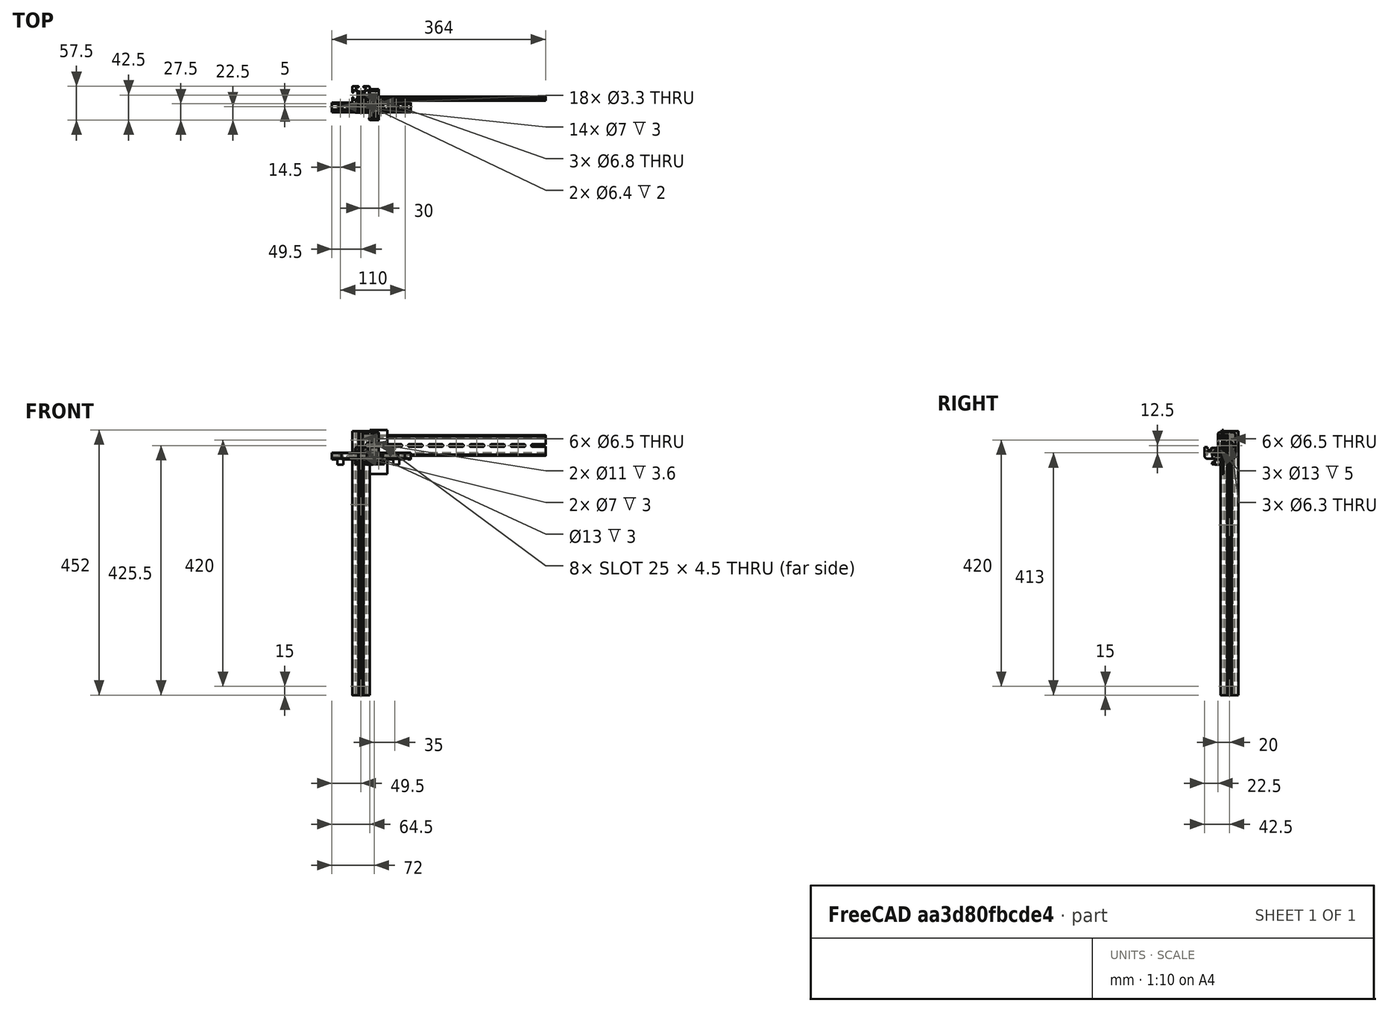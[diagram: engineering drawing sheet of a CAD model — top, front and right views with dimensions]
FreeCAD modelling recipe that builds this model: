
FCSTD DOCUMENT  (FreeCAD 0.19R24291 (Git))
Label: back-bottom-pannel
License: Other
LicenseURL: GPL3
objects: Part::Box×38, Part::Feature×36, Part::Cut×25, Part::MultiFuse×25, Part::Chamfer×19, Part::Cylinder×13, Part::Extrusion×7, Part::Refine×4
note: 167 computed .brp shape members not serialized (recipe doc carries the construction recipe); baked Part::Feature solids carry a one-line shape summary decoded from their .brp

FEATURE [Part::Box] Box  label="Cube"
  AttacherType = Attacher::AttachEngine3D
  Height = 45
  Length = 29
  Placement = pos=(-14,0,0) rot=(0,0,1;0rad)
  Width = 10
FEATURE [Part::Box] Box001  label="Cube001"
  AttacherType = Attacher::AttachEngine3D
  Height = 35.5
  Length = 29
  Placement = pos=(-11,2.5,4.75) rot=(0,0,1;0rad)
  Width = 7.5
FEATURE [Part::Cut] Cut
  Base = -> Box
  Tool = -> Box001
FEATURE [Part::Chamfer] Chamfer
  Base = -> Cut
  Edges = 5 edges r=2: [Edge1,Edge2,Edge4,Edge5,Edge7]
FEATURE [Part::Box] Box002  label="Cube002"
  AttacherType = Attacher::AttachEngine3D
  Height = 23
  Length = 27
  Placement = pos=(-12,2.5,11) rot=(0,0,1;0rad)
  Width = 6
FEATURE [Part::Chamfer] Chamfer001
  Base = -> Box002
  Edges = 2 edges r=1: [Edge11,Edge12]
FEATURE [Part::Box] Box003  label="Cube003"
  AttacherType = Attacher::AttachEngine3D
  Height = 4.75
  Length = 7.8
  Placement = pos=(-3.9,9,0) rot=(0,0,1;0rad)
  Width = 3
FEATURE [Part::Box] Box004  label="Cube004"
  AttacherType = Attacher::AttachEngine3D
  Height = 4.75
  Length = 7.8
  Placement = pos=(-3.9,9,40.25) rot=(0,0,1;0rad)
  Width = 3
FEATURE [Part::MultiFuse] Fusion
  Shapes = -> [Box004,Box003,Chamfer001]
FEATURE [Part::Chamfer] Chamfer002
  Base = -> Fusion
  Edges = 4 edges r=0.4: [Edge3,Edge7,Edge15,Edge19]
FEATURE [Part::MultiFuse] Fusion001
  Shapes = -> [Chamfer002,Chamfer]
FEATURE [Part::Cylinder] Cylinder
  Angle = 360
  AttacherType = Attacher::AttachEngine3D
  Height = 10
  Placement = pos=(0,5e-15,22.5) rot=(-1,0,0;1.5708rad)
  Radius = 2.15
FEATURE [Part::Cylinder] Cylinder001
  Angle = 360
  AttacherType = Attacher::AttachEngine3D
  Height = 10
  Placement = pos=(0,-6,22.5) rot=(-1,0,0;1.5708rad)
  Radius = 5.5
FEATURE [Part::Cut] Cut001
  Base = -> Fusion001
  Tool = -> Cylinder
FEATURE [Part::Cut] Cut002
  Base = -> Cut001
  Tool = -> Cylinder001
FEATURE [Part::Chamfer] Chamfer003
  Base = -> Cut002
  Edges = 1 edges r=0.4: [Edge82]
FEATURE [Part::Feature] Chamfer003001  label="Chamfer004"
  shape: bbox 29 x 12 x 45 mm, 39 faces (baked)
FEATURE [Part::Box] Box005  label="Cube005"
  AttacherType = Attacher::AttachEngine3D
  Height = 20
  Length = 35
  Placement = pos=(-25,0,0) rot=(0,0,1;0rad)
  Width = 5
FEATURE [Part::Cylinder] Cylinder002
  Angle = 360
  AttacherType = Attacher::AttachEngine3D
  Height = 10
  Placement = pos=(-15,-7,10) rot=(-1,0,0;1.5708rad)
  Radius = 6.5
FEATURE [Part::Box] Box006  label="Cube006"
  AttacherType = Attacher::AttachEngine3D
  Height = 20
  Length = 7.8
  Placement = pos=(-18.9,4,0) rot=(0,0,1;0rad)
  Width = 2
FEATURE [Part::Cylinder] Cylinder003
  Angle = 360
  AttacherType = Attacher::AttachEngine3D
  Height = 10
  Placement = pos=(-15,2e-15,10) rot=(-1,0,0;1.5708rad)
  Radius = 3.15
FEATURE [Part::Box] Box007  label="Cube007"
  AttacherType = Attacher::AttachEngine3D
  Height = 20
  Length = 9.5
  Placement = pos=(0.5,5,0) rot=(0,0,1;0rad)
  Width = 2
FEATURE [Part::Feature] Common001003002002001  label="din-309mm"
  Placement = pos=(147,-10,60.5) rot=(-1,0,0;1.5708rad)
  shape: bbox 305 x 7.5 x 35 mm, 68 faces (baked)
FEATURE [Part::Feature] Cut008004003004014002002002  label="3030-450mm-back002-drill"
  Placement = pos=(-15,20,-403) rot=(0,0,1;0rad)
  shape: bbox 30 x 30 x 450 mm, 181 faces (baked)
FEATURE [Part::Box] Box008  label="Cube008"
  AttacherType = Attacher::AttachEngine3D
  Height = 75
  Length = 30
  Placement = pos=(0,7,-26) rot=(0,0,1;0rad)
  Width = 3
FEATURE [Part::Box] Box009  label="Cube009"
  AttacherType = Attacher::AttachEngine3D
  Height = 45
  Length = 15
  Placement = pos=(0,10,0) rot=(0,0,1;0rad)
  Width = 20
FEATURE [Part::Box] Box010  label="Cube010"
  AttacherType = Attacher::AttachEngine3D
  Height = 23.5
  Length = 15
  Placement = pos=(0,11.75,10.75) rot=(0,0,1;0rad)
  Width = 7.75
FEATURE [Part::Box] Box011  label="Cube011"
  AttacherType = Attacher::AttachEngine3D
  Height = 35.5
  Length = 15
  Placement = pos=(0,10,4.75) rot=(0,0,1;0rad)
  Width = 7.75
FEATURE [Part::Box] Box012  label="Cube012"
  AttacherType = Attacher::AttachEngine3D
  Height = 4.75
  Length = 10
  Placement = pos=(-1,16.1,0) rot=(0,0,1;0rad)
  Width = 7.8
FEATURE [Part::Box] Box013  label="Cube013"
  AttacherType = Attacher::AttachEngine3D
  Height = 4.75
  Length = 10
  Placement = pos=(-1,16.1,40.25) rot=(0,0,1;0rad)
  Width = 7.8
FEATURE [Part::Box] Box014  label="Cube014"
  AttacherType = Attacher::AttachEngine3D
  Height = 23.5
  Length = 10
  Placement = pos=(-1,16.1,10.75) rot=(0,0,1;0rad)
  Width = 7.8
FEATURE [Part::MultiFuse] Fusion005
  Shapes = -> [Box014,Box012,Box013]
FEATURE [Part::Chamfer] Chamfer003008
  Base = -> Fusion005
  Edges = 6 edges r=1: [Edge2,Edge4,Edge14,Edge16,Edge26,Edge28]
FEATURE [Part::Cylinder] Cylinder004
  Angle = 360
  AttacherType = Attacher::AttachEngine3D
  Height = 18
  Placement = pos=(10,20,22.5) rot=(0,1,0;1.5708rad)
  Radius = 6.5
FEATURE [Part::Cylinder] Cylinder005
  Angle = 360
  AttacherType = Attacher::AttachEngine3D
  Height = 18
  Placement = pos=(-3.5,20,22.5) rot=(0,1,0;1.5708rad)
  Radius = 3.15
FEATURE [Part::Chamfer] Chamfer003009
  Base = -> Box005
  Edges = 4 edges r=2: [Edge2,Edge4,Edge6,Edge8]
FEATURE [Part::Chamfer] Chamfer003010
  Base = -> Box007
  Edges = 2 edges r=2: [Edge6,Edge8]
FEATURE [Part::Chamfer] Chamfer003011
  Base = -> Chamfer003009
  Edges = 8 edges r=1: [Edge1,Edge5,Edge6,Edge7,Edge8,Edge9,Edge10,Edge11]
FEATURE [Part::MultiFuse] Fusion007
  Shapes = -> [Chamfer003010,Chamfer003011,Box006]
FEATURE [Part::Feature] Cut008004003004014002002005003001  label="panel-inner-clip001"
  shape: bbox 35 x 7 x 20 mm, 27 faces (baked)
FEATURE [Part::Cut] Cut008004003004014002002005003002
  Base = -> Box009
  Tool = -> Box011
FEATURE [Part::MultiFuse] Fusion008
  Shapes = -> [Box010,Cut008004003004014002002005003002]
FEATURE [Part::Chamfer] Chamfer003012
  Base = -> Fusion008
  Edges = 4 edges r=0.4: [Edge39,Edge40,Edge41,Edge42]
FEATURE [Part::Chamfer] Chamfer003013
  Base = -> Chamfer003012
  Edges = 2 edges r=1: [Edge50,Edge54]
FEATURE [Part::Chamfer] Chamfer003014
  Base = -> Chamfer003013
  Edges = 2 edges r=3: [Edge57,Edge58]
FEATURE [Part::MultiFuse] Fusion009
  Shapes = -> [Chamfer003008,Chamfer003014]
FEATURE [Part::Cut] Cut008004003004014002002005003003
  Base = -> Fusion009
  Tool = -> Cylinder004
FEATURE [Part::Cut] Cut008004003004014002002005003004  label="din-stopper"
  Base = -> Cut008004003004014002002005003003
  Tool = -> Cylinder005
FEATURE [Part::Feature] Cut008004003004014002002005003004001  label="din-stopper001"
  shape: bbox 16 x 20 x 45 mm, 43 faces (baked)
FEATURE [Part::Box] Box015  label="Cube015"
  AttacherType = Attacher::AttachEngine3D
  Height = 15
  Length = 10
  Placement = pos=(-5,-10,0) rot=(0,0,1;0rad)
  Width = 4.5
FEATURE [Part::Box] Box016  label="Cube016"
  AttacherType = Attacher::AttachEngine3D
  Height = 5
  Length = 10
  Placement = pos=(-5,-9.5,0) rot=(0,0,1;0rad)
  Width = 16.5
FEATURE [Part::Box] Box017  label="Cube017"
  AttacherType = Attacher::AttachEngine3D
  Height = 2
  Length = 10
  Placement = pos=(-5,-3.9,-1) rot=(0,0,1;0rad)
  Width = 7.8
FEATURE [Part::Chamfer] Chamfer003015
  Base = -> Box017
  Edges = 1 edges r=1: [Edge9]
FEATURE [Part::Cylinder] Cylinder006
  Angle = 360
  AttacherType = Attacher::AttachEngine3D
  Height = 10
  Placement = pos=(0,0,-4) rot=(0,0,1;0rad)
  Radius = 1.65
FEATURE [Part::Cylinder] Cylinder007
  Angle = 360
  AttacherType = Attacher::AttachEngine3D
  Height = 10
  Placement = pos=(0,0,2) rot=(0,0,1;0rad)
  Radius = 3.5
FEATURE [Part::MultiFuse] Fusion011
  Shapes = -> [Cylinder007,Cylinder006]
FEATURE [Part::Cylinder] Cylinder008
  Angle = 360
  AttacherType = Attacher::AttachEngine3D
  Height = 10
  Placement = pos=(0,-12,10) rot=(-1,0,0;1.5708rad)
  Radius = 1.9
FEATURE [Part::Feature] Chamfer003017001_cs  label="gasket-support-profile"
  shape: bbox 3e-07 x 16.5 x 11 mm, 0 faces, 0 solids (baked)
FEATURE [Part::MultiFuse] Fusion012
  Shapes = -> [Box015,Box016,Chamfer003015]
FEATURE [Part::Chamfer] Chamfer003016
  Base = -> Fusion012
  Edges = 3 edges r=0.4: [Edge9,Edge16,Edge32]
FEATURE [Part::Chamfer] Chamfer003017
  Base = -> Chamfer003016
  Edges = 2 edges r=2: [Edge10,Edge27]
FEATURE [Part::Cut] Cut008004003004014002002005003004002
  Base = -> Chamfer003017
  Tool = -> Cylinder008
FEATURE [Part::Cut] Cut008004003004014002002005003004003  label="back-panel-support"
  Base = -> Cut008004003004014002002005003004002
  Tool = -> Fusion011
FEATURE [Part::Feature] Cut008004003004014002002005003004003001  label="back-panel-support001"
  shape: bbox 10 x 17 x 16 mm, 21 faces (baked)
FEATURE [Part::Feature] Chamfer003017001_cs001  label="gasket-support-profile001"
  shape: bbox 3e-07 x 16.5 x 11 mm, 0 faces, 0 solids (baked)
FEATURE [Part::Feature] Fusion011001  label="m3-slot"
  shape: bbox 7 x 7 x 16 mm, 5 faces (baked)
FEATURE [Part::Feature] Fusion011002  label="m3-slot001"
  shape: bbox 7 x 7 x 16 mm, 5 faces (baked)
FEATURE [Part::Feature] Fusion011003  label="m3-slot002"
  Placement = pos=(-50,0,0) rot=(0,0,1;0rad)
  shape: bbox 7 x 7 x 16 mm, 5 faces (baked)
FEATURE [Part::Feature] Fusion011004  label="m3-slot003"
  Placement = pos=(45,0,0) rot=(0,0,1;0rad)
  shape: bbox 7 x 7 x 16 mm, 5 faces (baked)
FEATURE [Part::Extrusion] Extrude
  Base = -> Chamfer003017001_cs001
  Dir = (1,0,0)
  DirMode = 2
  FaceMakerClass = Part::FaceMakerBullseye
  LengthFwd = 119
  LengthRev = 0
  Placement = pos=(-59.5,0,0) rot=(0,0,1;0rad)
  Solid = true
  Symmetric = false
FEATURE [Part::Feature] Chamfer003017001_cs002  label="gasket-support-profile002"
  shape: bbox 3e-07 x 16.5 x 11 mm, 0 faces, 0 solids (baked)
FEATURE [Part::Extrusion] Extrude001
  Base = -> Chamfer003017001_cs002
  Dir = (1,0,0)
  DirMode = 2
  FaceMakerClass = Part::FaceMakerBullseye
  LengthFwd = 39
  LengthRev = 0
  Placement = pos=(-19.5,0,0) rot=(0,0,1;0rad)
  Solid = true
  Symmetric = false
FEATURE [Part::Feature] Fusion011006  label="m3-slot004"
  Placement = pos=(-10,0,0) rot=(0,0,1;0rad)
  shape: bbox 7 x 7 x 16 mm, 5 faces (baked)
FEATURE [Part::Feature] Fusion011007  label="m3-slot005"
  Placement = pos=(10,0,0) rot=(0,0,1;0rad)
  shape: bbox 7 x 7 x 16 mm, 5 faces (baked)
FEATURE [Part::MultiFuse] Fusion011008
  Shapes = -> [Fusion011007,Fusion011006]
FEATURE [Part::Cut] Cut008004003004014002002005003004003002002  label="gasket-support-40mm"
  Base = -> Extrude001
  Tool = -> Fusion011008
FEATURE [Part::Feature] Chamfer003017001_cs003  label="gasket-support-profile003"
  shape: bbox 3e-07 x 16.5 x 11 mm, 0 faces, 0 solids (baked)
FEATURE [Part::Extrusion] Extrude002
  Base = -> Chamfer003017001_cs003
  Dir = (1,0,0)
  DirMode = 2
  FaceMakerClass = Part::FaceMakerBullseye
  LengthFwd = 44
  LengthRev = 0
  Placement = pos=(-17,0,0) rot=(0,0,1;0rad)
  Solid = true
  Symmetric = false
FEATURE [Part::Feature] Fusion011009  label="m3-slot006"
  Placement = pos=(15,0,0) rot=(0,0,1;0rad)
  shape: bbox 7 x 7 x 16 mm, 5 faces (baked)
FEATURE [Part::Feature] Fusion011010  label="m3-slot007"
  Placement = pos=(-15,0,0) rot=(0,0,1;0rad)
  shape: bbox 7 x 7 x 16 mm, 5 faces (baked)
FEATURE [Part::Cut] Cut008004003004014002002005003004003002003001002
  Base = -> Fusion007
  Tool = -> Cylinder003
FEATURE [Part::Cut] Cut008004003004014002002005003004003002003001003  label="back-btm-pannel-inner-clip"
  Base = -> Cut008004003004014002002005003004003002003001002
  Tool = -> Cylinder002
FEATURE [Part::Refine] Cut008004003004014002002005003004003002003001003001  label="back-btm-pannel-inner-clip001"
  Source = -> Cut008004003004014002002005003004003002003001003
FEATURE [Part::Feature] Cut008004003004014002002005003004003002003001003001001  label="back-btm-pannel-inner-clip002"
  shape: bbox 35 x 7 x 20 mm, 27 faces (baked)
FEATURE [Part::Box] Box018  label="Cube018"
  AttacherType = Attacher::AttachEngine3D
  Height = 5
  Length = 40
  Placement = pos=(-20,0,0) rot=(0,0,1;0rad)
  Width = 15
FEATURE [Part::Box] Box019  label="Cube019"
  AttacherType = Attacher::AttachEngine3D
  Height = 9
  Length = 40
  Placement = pos=(-20,12,1) rot=(0,0,1;0rad)
  Width = 4.5
FEATURE [Part::Chamfer] Chamfer003018
  Base = -> Box019
  Edges = 1 edges r=1.5: [Edge11]
FEATURE [Part::Chamfer] Chamfer003019
  Base = -> Chamfer003018
  Edges = 2 edges r=3: [Edge2,Edge11]
FEATURE [Part::Chamfer] Chamfer003020
  Base = -> Chamfer003019
  Edges = 5 edges r=1: [Edge3,Edge11,Edge15,Edge17,Edge18]
FEATURE [Part::Chamfer] Chamfer003021
  Base = -> Box018
  Edges = 2 edges r=2: [Edge1,Edge5]
FEATURE [Part::Chamfer] Chamfer003022
  Base = -> Chamfer003021
  Edges = 5 edges r=1: [Edge1,Edge5,Edge6,Edge7,Edge8]
FEATURE [Part::Cylinder] Cylinder009
  Angle = 360
  AttacherType = Attacher::AttachEngine3D
  Height = 10
  Placement = pos=(15,5,0) rot=(0,0,1;0rad)
  Radius = 1.65
FEATURE [Part::Cylinder] Cylinder010
  Angle = 360
  AttacherType = Attacher::AttachEngine3D
  Height = 10
  Placement = pos=(-15,5,0) rot=(0,0,1;0rad)
  Radius = 1.65
FEATURE [Part::MultiFuse] Fusion011012
  Shapes = -> [Chamfer003022,Chamfer003020]
FEATURE [Part::Cylinder] Cylinder011
  Angle = 360
  AttacherType = Attacher::AttachEngine3D
  Height = 10
  Placement = pos=(15,5,3) rot=(0,0,1;0rad)
  Radius = 3.2
FEATURE [Part::Cylinder] Cylinder012
  Angle = 360
  AttacherType = Attacher::AttachEngine3D
  Height = 10
  Placement = pos=(-15,5,3) rot=(0,0,1;0rad)
  Radius = 3.2
FEATURE [Part::MultiFuse] Fusion011013
  Shapes = -> [Cylinder012,Cylinder011,Cylinder010,Cylinder009]
FEATURE [Part::Cut] Cut008004003004014002002005003004003002003001003001002
  Base = -> Fusion011012
  Tool = -> Fusion011013
FEATURE [Part::Refine] Cut008004003004014002002005003004003002003001003001002001
  Source = -> Cut008004003004014002002005003004003002003001003001002
FEATURE [Part::Feature] Cut008004003004014002002005003004003002003001003001002001001
  shape: bbox 40 x 16.5 x 10 mm, 30 faces (baked)
FEATURE [Part::Feature] Extrude002001
  Placement = pos=(-27,0,0) rot=(0,0,1;0rad)
  shape: bbox 44 x 16.5 x 11 mm, 17 faces (baked)
FEATURE [Part::MultiFuse] Fusion011014
  Shapes = -> [Extrude002001,Extrude002]
FEATURE [Part::MultiFuse] Fusion011015
  Shapes = -> [Fusion011010,Fusion011009]
FEATURE [Part::Cut] Cut008004003004014002002005003004003002003001003001002001002  label="gasket-54mm"
  Base = -> Fusion011014
  Tool = -> Fusion011015
FEATURE [Part::Feature] Extrude002002
  Placement = pos=(-64.5,0,0) rot=(0,0,1;0rad)
  shape: bbox 119 x 16.5 x 11 mm, 17 faces (baked)
FEATURE [Part::MultiFuse] Fusion011016
  Shapes = -> [Extrude002002,Extrude]
FEATURE [Part::MultiFuse] Fusion011017
  Shapes = -> [Fusion011004,Fusion011002,Fusion011003]
FEATURE [Part::Cut] Cut008004003004014002002005003004003002003001003001002001002002  label="gasket-124mm"
  Base = -> Fusion011016
  Tool = -> Fusion011017
FEATURE [Part::Feature] Chamfer003017001_cs004  label="gasket-support-profile004"
  shape: bbox 3e-07 x 16.5 x 11 mm, 0 faces, 0 solids (baked)
FEATURE [Part::Extrusion] Extrude002003
  Base = -> Chamfer003017001_cs004
  Dir = (1,0,0)
  DirMode = 2
  FaceMakerClass = Part::FaceMakerBullseye
  LengthFwd = 38
  LengthRev = 0
  Placement = pos=(-19,0,0) rot=(0,0,1;0rad)
  Solid = true
  Symmetric = false
FEATURE [Part::Feature] Fusion011019  label="m3-slot009"
  Placement = pos=(10,0,0) rot=(0,0,1;0rad)
  shape: bbox 7 x 7 x 16 mm, 5 faces (baked)
FEATURE [Part::Feature] Fusion011020  label="m3-slot010"
  Placement = pos=(-10,0,0) rot=(0,0,1;0rad)
  shape: bbox 7 x 7 x 16 mm, 5 faces (baked)
FEATURE [Part::MultiFuse] Fusion011021
  Shapes = -> [Fusion011020,Fusion011019]
FEATURE [Part::Cut] Cut008004003004014002002005003004003002003001003001002001002002002  label="gasket-38mm"
  Base = -> Extrude002003
  Tool = -> Fusion011021
FEATURE [Part::Feature] Fusion011022  label="m3-slot011"
  shape: bbox 7 x 7 x 16 mm, 5 faces (baked)
FEATURE [Part::Feature] Chamfer003017001_cs005  label="gasket-support-profile005"
  shape: bbox 3e-07 x 16.5 x 11 mm, 0 faces, 0 solids (baked)
FEATURE [Part::Extrusion] Extrude002004
  Base = -> Chamfer003017001_cs005
  Dir = (1,0,0)
  DirMode = 2
  FaceMakerClass = Part::FaceMakerBullseye
  LengthFwd = 97
  LengthRev = 0
  Placement = pos=(-48.5,0,0) rot=(0,0,1;0rad)
  Solid = true
  Symmetric = false
FEATURE [Part::Feature] Fusion011023  label="m3-slot012"
  Placement = pos=(35,0,0) rot=(0,0,1;0rad)
  shape: bbox 7 x 7 x 16 mm, 5 faces (baked)
FEATURE [Part::Feature] Fusion011024  label="m3-slot013"
  Placement = pos=(-35,0,0) rot=(0,0,1;0rad)
  shape: bbox 7 x 7 x 16 mm, 5 faces (baked)
FEATURE [Part::MultiFuse] Fusion011025
  Shapes = -> [Fusion011023,Fusion011024,Fusion011022]
FEATURE [Part::Cut] Cut008004003004014002002005003004003002003001003001002001002002003  label="gasket-97mm"
  Base = -> Extrude002004
  Tool = -> Fusion011025
FEATURE [Part::Feature] Fusion011026  label="m3-slot014"
  Placement = pos=(3,0,0) rot=(0,0,1;0rad)
  shape: bbox 7 x 7 x 16 mm, 5 faces (baked)
FEATURE [Part::Feature] Chamfer003017001_cs006  label="gasket-support-profile006"
  shape: bbox 3e-07 x 16.5 x 11 mm, 0 faces, 0 solids (baked)
FEATURE [Part::Feature] Fusion011027  label="m3-slot015"
  Placement = pos=(19,0,0) rot=(0,0,1;0rad)
  shape: bbox 7 x 7 x 16 mm, 5 faces (baked)
FEATURE [Part::Extrusion] Extrude002005
  Base = -> Chamfer003017001_cs006
  Dir = (1,0,0)
  DirMode = 2
  FaceMakerClass = Part::FaceMakerBullseye
  LengthFwd = 22
  LengthRev = 0
  Solid = true
  Symmetric = false
FEATURE [Part::MultiFuse] Fusion011028
  Shapes = -> [Fusion011026,Fusion011027]
FEATURE [Part::Cut] Cut008004003004014002002005003004003002003001003001002001002002004  label="gasket-22mm"
  Base = -> Extrude002005
  Tool = -> Fusion011028
FEATURE [Part::Feature] Chamfer003017001_cs007  label="gasket-support-profile007"
  shape: bbox 3e-07 x 16.5 x 11 mm, 0 faces, 0 solids (baked)
FEATURE [Part::Extrusion] Extrude002006
  Base = -> Chamfer003017001_cs007
  Dir = (1,0,0)
  DirMode = 2
  FaceMakerClass = Part::FaceMakerBullseye
  LengthFwd = 70
  LengthRev = 0
  Solid = true
  Symmetric = false
FEATURE [Part::Feature] Fusion011029  label="m3-slot016"
  Placement = pos=(10,0,0) rot=(0,0,1;0rad)
  shape: bbox 7 x 7 x 16 mm, 5 faces (baked)
FEATURE [Part::Feature] Fusion011030  label="m3-slot017"
  Placement = pos=(60,0,0) rot=(0,0,1;0rad)
  shape: bbox 7 x 7 x 16 mm, 5 faces (baked)
FEATURE [Part::MultiFuse] Fusion011031
  Shapes = -> [Fusion011029,Fusion011030]
FEATURE [Part::Cut] Cut008004003004014002002005003004003002003001003001002001002002005  label="gasket-70mm"
  Base = -> Extrude002006
  Tool = -> Fusion011031
FEATURE [Part::Box] Box020  label="Cube020"
  AttacherType = Attacher::AttachEngine3D
  Height = 10
  Length = 10
  Placement = pos=(-5,-5,-10) rot=(0,0,1;0rad)
  Width = 10
FEATURE [Part::Box] Box021  label="Cube021"
  AttacherType = Attacher::AttachEngine3D
  Height = 10
  Length = 10
  Placement = pos=(30,-5,-10) rot=(0,0,1;0rad)
  Width = 10
FEATURE [Part::Box] Box022  label="Cube022"
  AttacherType = Attacher::AttachEngine3D
  Height = 10
  Length = 10
  Placement = pos=(55,-5,-10) rot=(0,0,1;0rad)
  Width = 10
FEATURE [Part::Box] Box023  label="Cube023"
  AttacherType = Attacher::AttachEngine3D
  Height = 10
  Length = 10
  Placement = pos=(5,-5,-10) rot=(0,0,1;0rad)
  Width = 10
FEATURE [Part::MultiFuse] Fusion011032
  Shapes = -> [Box023,Box022]
FEATURE [Part::Cut] Cut008004003004014002002005003004003002003001003001002001002002006  label="gasket-70mm-cut"
  Base = -> Cut008004003004014002002005003004003002003001003001002001002002005
  Tool = -> Fusion011032
FEATURE [Part::Box] Box024  label="Cube024"
  AttacherType = Attacher::AttachEngine3D
  Height = 10
  Length = 10
  Placement = pos=(-40,-5,-10) rot=(0,0,1;0rad)
  Width = 10
FEATURE [Part::MultiFuse] Fusion011033
  Shapes = -> [Box024,Box021,Box020]
FEATURE [Part::Cut] Cut008004003004014002002005003004003002003001003001002001002002007  label="gasket-97mm-cut"
  Base = -> Cut008004003004014002002005003004003002003001003001002001002002003
  Tool = -> Fusion011033
FEATURE [Part::Box] Box025  label="Cube025"
  AttacherType = Attacher::AttachEngine3D
  Height = 10
  Length = 10
  Placement = pos=(-55,-5,-10) rot=(0,0,1;0rad)
  Width = 10
FEATURE [Part::Box] Box026  label="Cube026"
  AttacherType = Attacher::AttachEngine3D
  Height = 10
  Length = 10
  Placement = pos=(40,-5,-10) rot=(0,0,1;0rad)
  Width = 10
FEATURE [Part::Box] Box027  label="Cube027"
  AttacherType = Attacher::AttachEngine3D
  Height = 10
  Length = 10
  Placement = pos=(-5,-5,-10) rot=(0,0,1;0rad)
  Width = 10
FEATURE [Part::Box] Box028  label="Cube028"
  AttacherType = Attacher::AttachEngine3D
  Height = 10
  Length = 10
  Placement = pos=(-55,-5,-10) rot=(0,0,1;0rad)
  Width = 10
FEATURE [Part::Box] Box029  label="Cube029"
  AttacherType = Attacher::AttachEngine3D
  Height = 10
  Length = 10
  Placement = pos=(40,-5,-10) rot=(0,0,1;0rad)
  Width = 10
FEATURE [Part::Box] Box030  label="Cube030"
  AttacherType = Attacher::AttachEngine3D
  Height = 10
  Length = 10
  Placement = pos=(-5,-5,-10) rot=(0,0,1;0rad)
  Width = 10
FEATURE [Part::MultiFuse] Fusion011034
  Shapes = -> [Box028,Box029,Box030]
FEATURE [Part::Cut] Cut008004003004014002002005003004003002003001003001002001002002008  label="gasket-124mm-cut"
  Base = -> Cut008004003004014002002005003004003002003001003001002001002002
  Tool = -> Fusion011034
FEATURE [Part::Box] Box031  label="Cube031"
  AttacherType = Attacher::AttachEngine3D
  Height = 10
  Length = 10
  Placement = pos=(10,-5,-10) rot=(0,0,1;0rad)
  Width = 10
FEATURE [Part::Box] Box032  label="Cube032"
  AttacherType = Attacher::AttachEngine3D
  Height = 10
  Length = 10
  Placement = pos=(-20,-5,-10) rot=(0,0,1;0rad)
  Width = 10
FEATURE [Part::MultiFuse] Fusion011035
  Shapes = -> [Box031,Box032]
FEATURE [Part::Cut] Cut008004003004014002002005003004003002003001003001002001002002009  label="gasket-54mm-cut"
  Base = -> Cut008004003004014002002005003004003002003001003001002001002
  Tool = -> Fusion011035
FEATURE [Part::Box] Box033  label="Cube033"
  AttacherType = Attacher::AttachEngine3D
  Height = 10
  Length = 10
  Placement = pos=(5,-5,-10) rot=(0,0,1;0rad)
  Width = 10
FEATURE [Part::Box] Box034  label="Cube034"
  AttacherType = Attacher::AttachEngine3D
  Height = 10
  Length = 10
  Placement = pos=(-15,-5,-10) rot=(0,0,1;0rad)
  Width = 10
FEATURE [Part::MultiFuse] Fusion011036
  Shapes = -> [Box033,Box034]
FEATURE [Part::Cut] Cut008004003004014002002005003004003002003001003001002001002002010  label="gasket-38mm-cut"
  Base = -> Cut008004003004014002002005003004003002003001003001002001002002002
  Tool = -> Fusion011036
FEATURE [Part::Box] Box035  label="Cube035"
  AttacherType = Attacher::AttachEngine3D
  Height = 10
  Length = 10
  Placement = pos=(-10,-5,5) rot=(0,0,1;0rad)
  Width = 10
FEATURE [Part::Feature] Fusion001001002  label="din-holder003"
  Placement = pos=(15,0,35) rot=(0,-1,0;1.5708rad)
  shape: bbox 16 x 45 x 20 mm, 55 faces (baked)
FEATURE [Part::Cut] Cut008004003004014002002005003004003002003001003001002001002002011  label="din-holder-cut"
  Base = -> Fusion001001002
  Tool = -> Box035
FEATURE [Part::Refine] Cut008004003004014002002005003004003002003001003001002001002002011001  label="din-holder-cut001"
  Source = -> Cut008004003004014002002005003004003002003001003001002001002002011
FEATURE [Part::Refine] Cut008004003004014002002005003004003002003001003001002001002002009001  label="gasket-54mm-cut001"
  Placement = pos=(0,0,0) rot=(1,0,0;1.5708rad)
  Source = -> Cut008004003004014002002005003004003002003001003001002001002002009
FEATURE [Part::Box] Box036  label="Cube036"
  AttacherType = Attacher::AttachEngine3D
  Height = 22
  Length = 10
  Placement = pos=(25,-16,-12) rot=(0,0,1;0rad)
  Width = 24
FEATURE [Part::Box] Box037  label="Cube037"
  AttacherType = Attacher::AttachEngine3D
  Height = 22
  Length = 10
  Placement = pos=(-35,-16,-12) rot=(0,0,1;0rad)
  Width = 24
FEATURE [Part::MultiFuse] Fusion001001003
  Shapes = -> [Box037,Box036]
FEATURE [Part::Cut] Cut008004003004014002002005003004003002003001003001002001002002011002  label="gasket-50mm-cut"
  Base = -> Cut008004003004014002002005003004003002003001003001002001002002009001
  Tool = -> Fusion001001003
